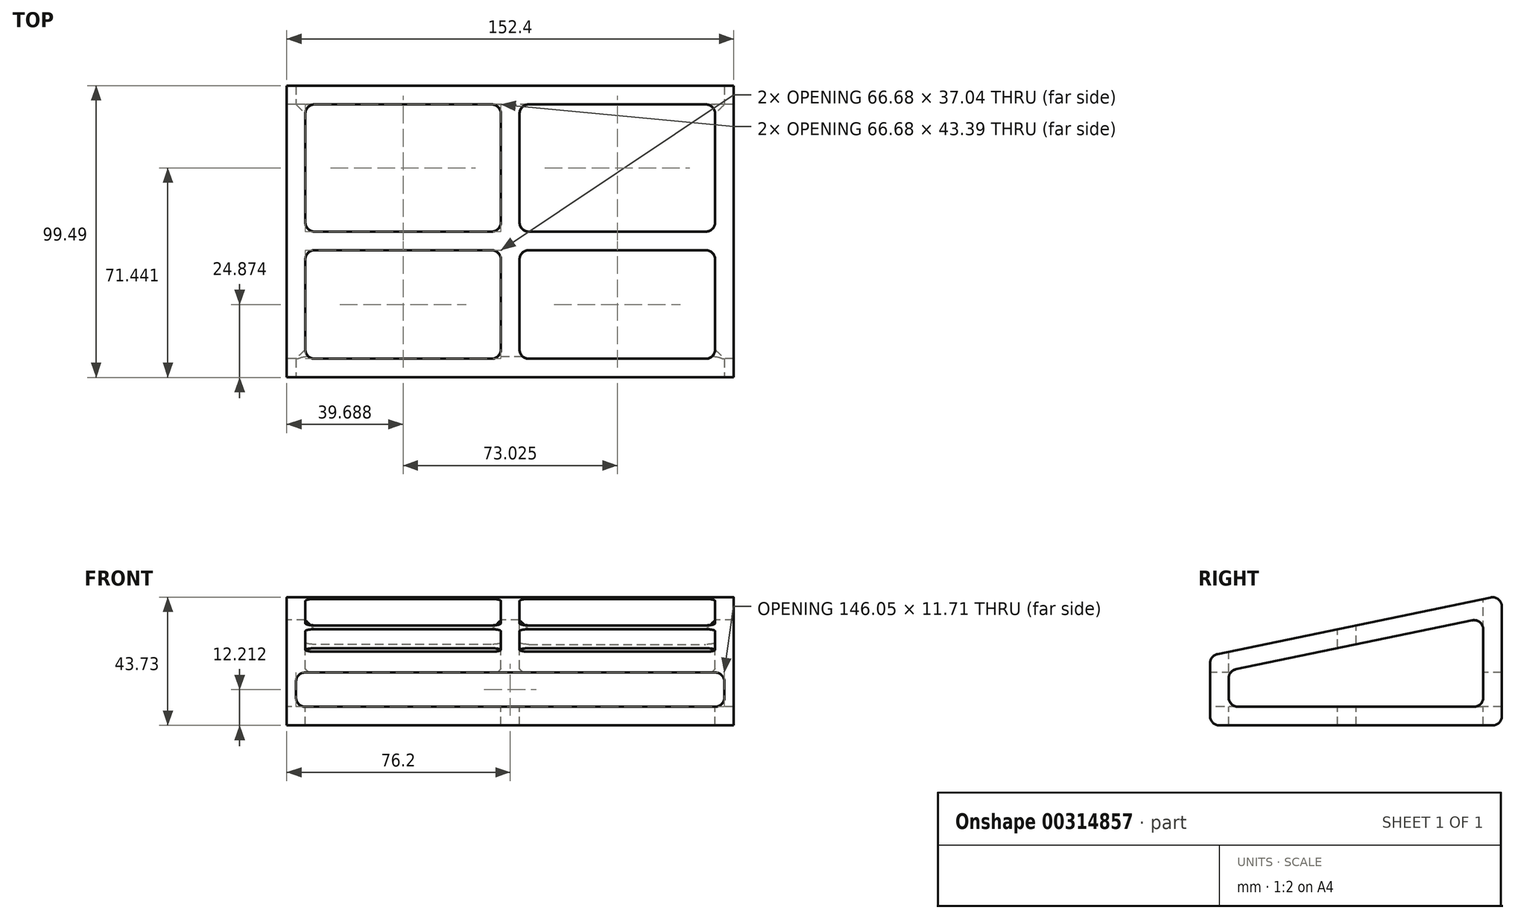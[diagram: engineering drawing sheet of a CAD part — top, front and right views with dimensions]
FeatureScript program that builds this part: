
annotation { "Feature Type Name" : "Feature", "Feature Type Description" : "" }
export const myFeature = defineFeature(function(context is Context, id is Id, definition is map)
    precondition{}
    {
        {
            var Q0;
            Q0=qCreatedBy(makeId("Right.planeOp"),FACE);
            var sketch = newSketch(context, id + "F0", { "sketchPlane" : qUnion([Q0])});
            skLineSegment(sketch, "E0", {"start": v(40.86, -31.3) * mm, "end": v(-52.27, -31.3) * mm});
            skLineSegment(sketch, "E1", {"start": v(-45.92, -24.96) * mm, "end": v(34.51, -24.96) * mm});
            skLineSegment(sketch, "E2", {"start": v(37.69, -21.78) * mm, "end": v(37.69, 1.44) * mm});
            skLineSegment(sketch, "E3", {"start": v(33.87, 4.55) * mm, "end": v(-46.57, -12.13) * mm});
            skLineSegment(sketch, "E4", {"start": v(-52.92, -6.96) * mm, "end": v(40.22, 12.35) * mm});
            skLineSegment(sketch, "E5", {"start": v(44.04, 9.24) * mm, "end": v(44.04, -28.13) * mm});
            skLineSegment(sketch, "E6", {"start": v(-49.1, -15.23) * mm, "end": v(-49.1, -21.78) * mm});
            skLineSegment(sketch, "E7", {"start": v(-55.45, -10.07) * mm, "end": v(-55.45, -28.13) * mm});
            skLineSegment(sketch, "E8", {"start": v(37.69, 5.34) * mm, "end": v(36.4, 11.56) * mm, "construction": true});
            skLineSegment(sketch, "E9", {"start": v(20.4, -24.96) * mm, "end": v(20.4, -31.3) * mm, "construction": true});
            skPoint(sketch, "E10.visualSharp", {"position": v(-55.45, -7.48) * mm});
            skArc(sketch, "E10.filletArc", {"start": v(-52.92, -6.96) * mm, "mid": v(-54.73, -8.06) * mm, "end": v(-55.45, -10.07) * mm});
            skPoint(sketch, "E11.visualSharp", {"position": v(44.04, 13.14) * mm});
            skArc(sketch, "E11.filletArc", {"start": v(44.04, 9.24) * mm, "mid": v(42.87, 11.7) * mm, "end": v(40.22, 12.35) * mm});
            skPoint(sketch, "E12.visualSharp", {"position": v(37.69, 5.34) * mm});
            skArc(sketch, "E12.filletArc", {"start": v(37.69, 1.44) * mm, "mid": v(36.52, 3.9) * mm, "end": v(33.87, 4.55) * mm});
            skPoint(sketch, "E13.visualSharp", {"position": v(-49.1, -12.65) * mm});
            skArc(sketch, "E13.filletArc", {"start": v(-46.57, -12.13) * mm, "mid": v(-48.38, -13.23) * mm, "end": v(-49.1, -15.23) * mm});
            skPoint(sketch, "E14.visualSharp", {"position": v(-49.1, -24.96) * mm});
            skArc(sketch, "E14.filletArc", {"start": v(-49.1, -21.78) * mm, "mid": v(-48.17, -24.03) * mm, "end": v(-45.92, -24.96) * mm});
            skPoint(sketch, "E15.visualSharp", {"position": v(37.69, -24.96) * mm});
            skArc(sketch, "E15.filletArc", {"start": v(34.51, -24.96) * mm, "mid": v(36.76, -24.03) * mm, "end": v(37.69, -21.78) * mm});
            skPoint(sketch, "E16.visualSharp", {"position": v(-55.45, -31.3) * mm});
            skArc(sketch, "E16.filletArc", {"start": v(-55.45, -28.13) * mm, "mid": v(-54.52, -30.38) * mm, "end": v(-52.27, -31.3) * mm});
            skPoint(sketch, "E17.visualSharp", {"position": v(44.04, -31.3) * mm});
            skArc(sketch, "E17.filletArc", {"start": v(40.86, -31.3) * mm, "mid": v(43.1, -30.38) * mm, "end": v(44.04, -28.13) * mm});
            skSolve(sketch);
        }
        {
            var Q0;
            Q0=makeQuery(id+"F0.imprint","IMPRINT",FACE,{"disambiguationData":[TD([[makeQuery(id+"F0.imprint","IMPRINT",EDGE,{"derivedFrom":sQuery(id+"F0.wireOp",EDGE,"E0")}),-1.0]])]});
            extrude(context, id + "F1", {"entities" : qUnion([Q0]), "depth" : 152.4 * mm});
        }
        {
            var Q0;
            Q0=qCreatedBy(makeId("Top.planeOp"),FACE);
            var sketch = newSketch(context, id + "F2", { "sketchPlane" : qUnion([Q0])});
            skLineSegment(sketch, "E18.bottom", {"start": v(9.53, 37.69) * mm, "end": v(69.85, 37.69) * mm});
            skLineSegment(sketch, "E18.top", {"start": v(9.53, -5.7) * mm, "end": v(69.85, -5.7) * mm});
            skLineSegment(sketch, "E18.left", {"start": v(6.35, 34.51) * mm, "end": v(6.35, -2.53) * mm});
            skLineSegment(sketch, "E18.right", {"start": v(73.03, 34.51) * mm, "end": v(73.03, -2.53) * mm});
            skLineSegment(sketch, "E19.bottom", {"start": v(9.52, -12.05) * mm, "end": v(69.85, -12.05) * mm});
            skLineSegment(sketch, "E19.top", {"start": v(9.52, -49.1) * mm, "end": v(69.85, -49.1) * mm});
            skLineSegment(sketch, "E19.left", {"start": v(6.35, -15.23) * mm, "end": v(6.35, -45.92) * mm});
            skLineSegment(sketch, "E19.right", {"start": v(73.03, -15.23) * mm, "end": v(73.03, -45.92) * mm});
            skLineSegment(sketch, "E20", {"start": v(76.2, 52.97) * mm, "end": v(76.2, -75.5) * mm, "construction": true});
            skLineSegment(sketch, "E21.MirrorCS", {"start": v(146.05, 34.51) * mm, "end": v(146.05, -2.53) * mm});
            skLineSegment(sketch, "E22.MirrorCS", {"start": v(142.88, -5.7) * mm, "end": v(82.55, -5.7) * mm});
            skLineSegment(sketch, "E23.MirrorCS", {"start": v(142.87, 37.69) * mm, "end": v(82.55, 37.69) * mm});
            skLineSegment(sketch, "E24.MirrorCS", {"start": v(79.38, 34.51) * mm, "end": v(79.38, -2.53) * mm});
            skLineSegment(sketch, "E25", {"start": v(-19.66, -4.65) * mm, "end": v(156.32, -4.65) * mm});
            skLineSegment(sketch, "E26.MirrorCS", {"start": v(79.38, -15.23) * mm, "end": v(79.38, -45.92) * mm});
            skLineSegment(sketch, "E27.MirrorCS", {"start": v(146.05, -15.23) * mm, "end": v(146.05, -45.92) * mm});
            skLineSegment(sketch, "E28.MirrorCS", {"start": v(142.88, -12.05) * mm, "end": v(82.55, -12.05) * mm});
            skLineSegment(sketch, "E29.MirrorCS", {"start": v(142.88, -49.1) * mm, "end": v(82.55, -49.1) * mm});
            skPoint(sketch, "E30.visualSharp", {"position": v(6.35, 37.69) * mm});
            skArc(sketch, "E30.filletArc", {"start": v(9.53, 37.69) * mm, "mid": v(7.28, 36.76) * mm, "end": v(6.35, 34.51) * mm});
            skPoint(sketch, "E31.visualSharp", {"position": v(73.03, 37.69) * mm});
            skArc(sketch, "E31.filletArc", {"start": v(73.03, 34.51) * mm, "mid": v(72.1, 36.76) * mm, "end": v(69.85, 37.69) * mm});
            skPoint(sketch, "E32.visualSharp", {"position": v(73.03, -12.05) * mm});
            skArc(sketch, "E32.filletArc", {"start": v(73.03, -15.23) * mm, "mid": v(72.1, -12.98) * mm, "end": v(69.85, -12.05) * mm});
            skPoint(sketch, "E33.visualSharp", {"position": v(6.35, -12.05) * mm});
            skArc(sketch, "E33.filletArc", {"start": v(9.52, -12.05) * mm, "mid": v(7.28, -12.98) * mm, "end": v(6.35, -15.23) * mm});
            skPoint(sketch, "E34.visualSharp", {"position": v(6.35, -49.1) * mm});
            skArc(sketch, "E34.filletArc", {"start": v(6.35, -45.92) * mm, "mid": v(7.28, -48.17) * mm, "end": v(9.53, -49.1) * mm});
            skPoint(sketch, "E35.visualSharp", {"position": v(73.03, -49.1) * mm});
            skArc(sketch, "E35.filletArc", {"start": v(69.85, -49.1) * mm, "mid": v(72.1, -48.17) * mm, "end": v(73.03, -45.92) * mm});
            skPoint(sketch, "E36.visualSharp", {"position": v(79.38, -49.1) * mm});
            skArc(sketch, "E36.filletArc", {"start": v(79.38, -45.92) * mm, "mid": v(80.3, -48.17) * mm, "end": v(82.55, -49.1) * mm});
            skPoint(sketch, "E37.visualSharp", {"position": v(79.38, -12.05) * mm});
            skArc(sketch, "E37.filletArc", {"start": v(82.55, -12.05) * mm, "mid": v(80.3, -12.98) * mm, "end": v(79.38, -15.23) * mm});
            skPoint(sketch, "E38.visualSharp", {"position": v(146.05, -12.05) * mm});
            skArc(sketch, "E38.filletArc", {"start": v(146.05, -15.23) * mm, "mid": v(145.12, -12.98) * mm, "end": v(142.88, -12.05) * mm});
            skPoint(sketch, "E39.visualSharp", {"position": v(146.05, -49.1) * mm});
            skArc(sketch, "E39.filletArc", {"start": v(142.88, -49.1) * mm, "mid": v(145.12, -48.17) * mm, "end": v(146.05, -45.92) * mm});
            skPoint(sketch, "E40.visualSharp", {"position": v(146.05, -5.7) * mm});
            skArc(sketch, "E40.filletArc", {"start": v(142.88, -5.7) * mm, "mid": v(145.12, -4.77) * mm, "end": v(146.05, -2.53) * mm});
            skPoint(sketch, "E41.visualSharp", {"position": v(79.38, -5.7) * mm});
            skArc(sketch, "E41.filletArc", {"start": v(79.38, -2.53) * mm, "mid": v(80.3, -4.77) * mm, "end": v(82.55, -5.7) * mm});
            skPoint(sketch, "E42.visualSharp", {"position": v(79.37, 37.69) * mm});
            skArc(sketch, "E42.filletArc", {"start": v(82.55, 37.69) * mm, "mid": v(80.3, 36.76) * mm, "end": v(79.38, 34.51) * mm});
            skPoint(sketch, "E43.visualSharp", {"position": v(146.05, 37.69) * mm});
            skArc(sketch, "E43.filletArc", {"start": v(146.05, 34.51) * mm, "mid": v(145.12, 36.76) * mm, "end": v(142.87, 37.69) * mm});
            skPoint(sketch, "E44.visualSharp", {"position": v(73.03, -5.7) * mm});
            skArc(sketch, "E44.filletArc", {"start": v(69.85, -5.7) * mm, "mid": v(72.1, -4.77) * mm, "end": v(73.03, -2.53) * mm});
            skPoint(sketch, "E45.visualSharp", {"position": v(6.35, -5.7) * mm});
            skArc(sketch, "E45.filletArc", {"start": v(6.35, -2.53) * mm, "mid": v(7.28, -4.77) * mm, "end": v(9.53, -5.7) * mm});
            skSolve(sketch);
        }
        {
            var Q0;
            Q0 = qSketchRegion(id + "F2", true);
            extrude(context, id + "F3", {"entities" : qUnion([Q0]), "operationType" : NewBodyOperationType.REMOVE, "endBound" : BoundingType.THROUGH_ALL, "oppositeDirection" : true, "depth" : 15.24 * mm, "hasSecondDirection" : true, "secondDirectionBound" : SecondDirectionBoundingType.THROUGH_ALL, "secondDirectionOppositeDirection" : false, "secondDirectionDepth" : 25.4 * mm});
        }
        {
            var Q0;
            Q0=qCreatedBy(makeId("Front.planeOp"),FACE);
            var sketch = newSketch(context, id + "F4", { "sketchPlane" : qUnion([Q0])});
            skLineSegment(sketch, "E46.bottom", {"start": v(6.35, -13.24) * mm, "end": v(146.05, -13.24) * mm});
            skLineSegment(sketch, "E46.top", {"start": v(6.35, -24.96) * mm, "end": v(146.05, -24.96) * mm});
            skLineSegment(sketch, "E46.left", {"start": v(3.17, -16.42) * mm, "end": v(3.17, -21.78) * mm});
            skLineSegment(sketch, "E46.right", {"start": v(149.22, -16.42) * mm, "end": v(149.22, -21.78) * mm});
            skPoint(sketch, "E47.visualSharp", {"position": v(3.17, -13.24) * mm});
            skArc(sketch, "E47.filletArc", {"start": v(6.35, -13.24) * mm, "mid": v(4.1, -14.17) * mm, "end": v(3.17, -16.42) * mm});
            skPoint(sketch, "E48.visualSharp", {"position": v(3.17, -24.96) * mm});
            skArc(sketch, "E48.filletArc", {"start": v(3.18, -21.78) * mm, "mid": v(4.1, -24.03) * mm, "end": v(6.35, -24.96) * mm});
            skPoint(sketch, "E49.visualSharp", {"position": v(149.22, -13.24) * mm});
            skArc(sketch, "E49.filletArc", {"start": v(149.22, -16.42) * mm, "mid": v(148.3, -14.17) * mm, "end": v(146.05, -13.24) * mm});
            skPoint(sketch, "E50.visualSharp", {"position": v(149.22, -24.96) * mm});
            skArc(sketch, "E50.filletArc", {"start": v(146.05, -24.96) * mm, "mid": v(148.3, -24.03) * mm, "end": v(149.23, -21.78) * mm});
            skLineSegment(sketch, "E51", {"start": v(158.45, -9.48) * mm, "end": v(-20.87, -9.48) * mm, "construction": true});
            skLineSegment(sketch, "E52", {"start": v(76.2, -9.48) * mm, "end": v(76.2, 12.35) * mm, "construction": true});
            skLineSegment(sketch, "E53", {"start": v(116.85, -9.48) * mm, "end": v(116.85, -31.3) * mm, "construction": true});
            skArc(sketch, "E54.MirrorCS", {"start": v(3.18, 2.83) * mm, "mid": v(4.1, 5.07) * mm, "end": v(6.35, 6) * mm});
            skLineSegment(sketch, "E55.MirrorCS", {"start": v(3.17, -2.54) * mm, "end": v(3.17, 2.83) * mm});
            skArc(sketch, "E56.MirrorCS", {"start": v(6.35, -5.71) * mm, "mid": v(4.1, -4.78) * mm, "end": v(3.17, -2.54) * mm});
            skArc(sketch, "E57.MirrorCS", {"start": v(149.22, -2.54) * mm, "mid": v(148.3, -4.78) * mm, "end": v(146.05, -5.71) * mm});
            skArc(sketch, "E58.MirrorCS", {"start": v(146.05, 6) * mm, "mid": v(148.3, 5.07) * mm, "end": v(149.23, 2.83) * mm});
            skLineSegment(sketch, "E59.MirrorCS", {"start": v(149.22, -2.54) * mm, "end": v(149.22, 2.83) * mm});
            skLineSegment(sketch, "E60.MirrorCS", {"start": v(6.35, 6) * mm, "end": v(146.05, 6) * mm});
            skLineSegment(sketch, "E61.MirrorCS", {"start": v(6.35, -5.71) * mm, "end": v(146.05, -5.71) * mm});
            skSolve(sketch);
        }
        {
            var Q0;
            Q0=makeQuery(id+"F4.imprint","IMPRINT",FACE,{"disambiguationData":[TD([[makeQuery(id+"F4.imprint","IMPRINT",EDGE,{"derivedFrom":sQuery(id+"F4.wireOp",EDGE,"E46.bottom")}),-1.0]])]});
            extrude(context, id + "F5", {"entities" : qUnion([Q0]), "operationType" : NewBodyOperationType.REMOVE, "endBound" : BoundingType.THROUGH_ALL, "oppositeDirection" : true, "depth" : 25.4 * mm, "hasSecondDirection" : true, "secondDirectionBound" : SecondDirectionBoundingType.THROUGH_ALL, "secondDirectionOppositeDirection" : false, "secondDirectionDepth" : 25.4 * mm});
        }
    });
